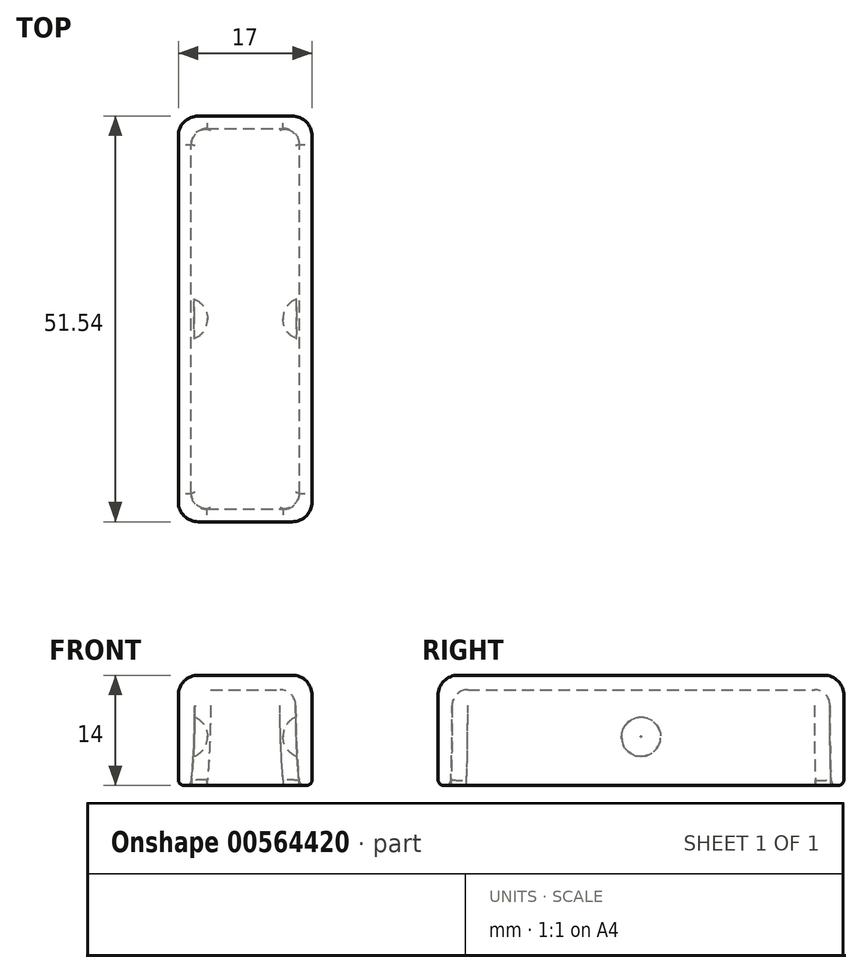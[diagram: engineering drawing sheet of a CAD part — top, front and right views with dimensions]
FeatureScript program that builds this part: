
annotation { "Feature Type Name" : "Feature", "Feature Type Description" : "" }
export const myFeature = defineFeature(function(context is Context, id is Id, definition is map)
    precondition{}
    {
        {
            var Q0;
            Q0=qCreatedBy(makeId("Top.planeOp"),FACE);
            var sketch = newSketch(context, id + "F0", { "sketchPlane" : qUnion([Q0])});
            skLineSegment(sketch, "E0.bottom", {"start": v(39.5, 39.5) * mm, "end": v(-39.5, 39.5) * mm});
            skLineSegment(sketch, "E0.top", {"start": v(39.5, -39.5) * mm, "end": v(-39.5, -39.5) * mm});
            skLineSegment(sketch, "E0.left", {"start": v(39.5, 39.5) * mm, "end": v(39.5, -39.5) * mm});
            skLineSegment(sketch, "E0.right", {"start": v(-39.5, 39.5) * mm, "end": v(-39.5, -39.5) * mm});
            skPoint(sketch, "E0.middle", {"position": v(0, 0) * mm});
            skSolve(sketch);
        }
        {
            var Q0;
            Q0=qSketchRegion(id+"F0",true);
            extrude(context, id + "F1", {"entities" : qUnion([Q0]), "depth" : 50.8 * mm, "offsetDistance" : 25.4 * mm});
        }
        {
            var Q0;
            Q0=makeQuery(id+"F1.opExtrude","SWEPT_FACE",FACE,{"disambiguationData":[OSD([sQuery(id+"F0.wireOp",EDGE,"E0.bottom")])]});
            var sketch = newSketch(context, id + "F2", { "sketchPlane" : qUnion([Q0])});
            skFitSpline(sketch, "E1", {"points": [v(-6.4, 50.8) * mm, v(-11.41, 24.4) * mm, v(-39.5, 10) * mm], "startDerivative": vector(0.05, -69.07) * mm, "endDerivative": vector(-77.08, -18.22) * mm});
            skLineSegment(sketch, "E2", {"start": v(-6.4, 50.8) * mm, "end": v(-39.5, 50.8) * mm});
            skLineSegment(sketch, "E3", {"start": v(-39.5, 50.8) * mm, "end": v(-39.5, 10) * mm});
            skFitSpline(sketch, "E4.MirrorCS", {"points": [v(6.4, 50.8) * mm, v(11.41, 24.4) * mm, v(39.5, 10) * mm], "startDerivative": vector(-0.05, -69.07) * mm, "endDerivative": vector(77.08, -18.22) * mm});
            skLineSegment(sketch, "E5.MirrorCS", {"start": v(6.4, 50.8) * mm, "end": v(39.5, 50.8) * mm});
            skLineSegment(sketch, "E6.MirrorCS", {"start": v(39.5, 50.8) * mm, "end": v(39.5, 10) * mm});
            skSolve(sketch);
        }
        {
            var Q0;
            Q0=qSketchRegion(id+"F2",true);
            extrude(context, id + "F3", {"entities" : qUnion([Q0]), "operationType" : NewBodyOperationType.REMOVE, "endBound" : BoundingType.THROUGH_ALL, "oppositeDirection" : true, "depth" : 25.4 * mm, "offsetDistance" : 25.4 * mm});
        }
        {
            var Q0;
            Q0=makeQuery(id+"F1.opExtrude","CAP_FACE",FACE,{"disambiguationData":[OSD([sQuery(id+"F0.wireOp",EDGE,"E0.bottom"),sQuery(id+"F0.wireOp",EDGE,"E0.top"),sQuery(id+"F0.wireOp",EDGE,"E0.left"),sQuery(id+"F0.wireOp",EDGE,"E0.right")])],"isStart":true});
            var sketch = newSketch(context, id + "F4", { "sketchPlane" : qUnion([Q0])});
            skCircle(sketch, "E7", {"center": v(0, 0) * mm, "radius": 39.5 * mm});
            skSolve(sketch);
        }
        {
            var Q0;
            {var subQ0=sQuery(id+"F4.wireOp",EDGE,"E7");var subQ1=makeQuery(id+"F1.opExtrude","CAP_EDGE",EDGE,{"disambiguationData":[OSD([sQuery(id+"F0.wireOp",EDGE,"E0.left")])],"isStart":true});var subQ2=makeQuery(id+"F4.imprint","INTERSECT",VERTEX,{"derivedFrom":[subQ1,subQ0]});Q0=makeQuery(id+"F4.imprint","IMPRINT",FACE,{"disambiguationData":[TD([[makeQuery(id+"F4.imprint","IMPRINT",EDGE,{"disambiguationData":[TD([[subQ2,1.0]])],"derivedFrom":subQ0}),-1.0]])]});}
            var Q1;
            {var subQ0=sQuery(id+"F4.wireOp",EDGE,"E7");var subQ1=makeQuery(id+"F1.opExtrude","CAP_EDGE",EDGE,{"disambiguationData":[OSD([sQuery(id+"F0.wireOp",EDGE,"E0.right")])],"isStart":true});var subQ2=makeQuery(id+"F4.imprint","INTERSECT",VERTEX,{"derivedFrom":[subQ1,subQ0]});Q1=makeQuery(id+"F4.imprint","IMPRINT",FACE,{"disambiguationData":[TD([[makeQuery(id+"F4.imprint","IMPRINT",EDGE,{"disambiguationData":[TD([[subQ2,-1.0]])],"derivedFrom":subQ0}),-1.0]])]});}
            var Q2;
            {var subQ0=sQuery(id+"F4.wireOp",EDGE,"E7");var subQ1=makeQuery(id+"F1.opExtrude","CAP_EDGE",EDGE,{"disambiguationData":[OSD([sQuery(id+"F0.wireOp",EDGE,"E0.top")])],"isStart":true});var subQ2=makeQuery(id+"F4.imprint","INTERSECT",VERTEX,{"derivedFrom":[subQ1,subQ0]});Q2=makeQuery(id+"F4.imprint","IMPRINT",FACE,{"disambiguationData":[TD([[makeQuery(id+"F4.imprint","IMPRINT",EDGE,{"disambiguationData":[TD([[subQ2,1.0]])],"derivedFrom":subQ0}),-1.0]])]});}
            var Q3;
            {var subQ0=sQuery(id+"F4.wireOp",EDGE,"E7");var subQ1=makeQuery(id+"F1.opExtrude","CAP_EDGE",EDGE,{"disambiguationData":[OSD([sQuery(id+"F0.wireOp",EDGE,"E0.top")])],"isStart":true});var subQ2=makeQuery(id+"F4.imprint","INTERSECT",VERTEX,{"derivedFrom":[subQ1,subQ0]});Q3=makeQuery(id+"F4.imprint","IMPRINT",FACE,{"disambiguationData":[TD([[makeQuery(id+"F4.imprint","IMPRINT",EDGE,{"disambiguationData":[TD([[subQ2,-1.0]])],"derivedFrom":subQ0}),-1.0]])]});}
            extrude(context, id + "F5", {"entities" : qUnion([Q0, Q1, Q2, Q3]), "operationType" : NewBodyOperationType.REMOVE, "endBound" : BoundingType.THROUGH_ALL, "oppositeDirection" : true, "depth" : 25.4 * mm, "offsetDistance" : 25.4 * mm});
        }
        {
            var Q0;
            Q0=qCreatedBy(makeId("Right.planeOp"),FACE);
            var sketch = newSketch(context, id + "F6", { "sketchPlane" : qUnion([Q0])});
            skLineSegment(sketch, "E8.top", {"start": v(24, 50.26) * mm, "end": v(-24, 50.26) * mm});
            skPoint(sketch, "E8.middle", {"position": v(0, 47.85) * mm});
            skPoint(sketch, "E8.bottom.end.orphan", {"position": v(-24, 45.43) * mm});
            skPoint(sketch, "E8.left.start.orphan", {"position": v(24, 45.43) * mm});
            skFitSpline(sketch, "E9", {"points": [v(-24, 50.26) * mm, v(-27.02, 23.49) * mm, v(-39.57, 10) * mm], "startDerivative": vector(-0.16, -57.64) * mm, "endDerivative": vector(-33.37, -21.46) * mm});
            skLineSegment(sketch, "E10", {"start": v(-40.45, 52.33) * mm, "end": v(-43.17, 14.06) * mm});
            skLineSegment(sketch, "E11", {"start": v(-43.17, 14.06) * mm, "end": v(-39.57, 10) * mm});
            skFitSpline(sketch, "E12.MirrorCS", {"points": [v(24, 50.26) * mm, v(27.02, 23.49) * mm, v(39.57, 10) * mm], "startDerivative": vector(0.16, -57.64) * mm, "endDerivative": vector(33.37, -21.46) * mm});
            skLineSegment(sketch, "E13.MirrorCS", {"start": v(40.45, 52.33) * mm, "end": v(43.17, 14.06) * mm});
            skLineSegment(sketch, "E14.MirrorCS", {"start": v(43.17, 14.06) * mm, "end": v(39.57, 10) * mm});
            skLineSegment(sketch, "E15", {"start": v(40.45, 52.33) * mm, "end": v(24, 52.33) * mm});
            skLineSegment(sketch, "E16", {"start": v(24, 52.33) * mm, "end": v(24, 50.26) * mm});
            skLineSegment(sketch, "E17", {"start": v(-24, 52.33) * mm, "end": v(-40.45, 52.33) * mm});
            skLineSegment(sketch, "E18", {"start": v(-24, 52.33) * mm, "end": v(-24, 50.26) * mm});
            skLineSegment(sketch, "E19", {"start": v(-24, 52.33) * mm, "end": v(24, 52.33) * mm});
            skSolve(sketch);
        }
        {
            var Q0;
            Q0=qSketchRegion(id+"F6",true);
            extrude(context, id + "F7", {"entities" : qUnion([Q0]), "operationType" : NewBodyOperationType.REMOVE, "endBound" : BoundingType.THROUGH_ALL, "oppositeDirection" : true, "depth" : 25.4 * mm, "offsetDistance" : 25.4 * mm, "hasSecondDirection" : true, "secondDirectionBound" : SecondDirectionBoundingType.THROUGH_ALL, "secondDirectionOppositeDirection" : false, "secondDirectionDepth" : 25.4 * mm});
        }
        {
            var Q0;
            Q0=makeQuery(id+"F3.boolean.opBoolean","COPY",FACE,{"derivedFrom":makeQuery(id+"F3.opExtrude","SWEPT_FACE",FACE,{"disambiguationData":[OSD([sQuery(id+"F2.wireOp",EDGE,"E4.MirrorCS")])]})});
            var Q1;
            Q1=makeQuery(id+"F7.boolean.opBoolean","COPY",FACE,{"derivedFrom":makeQuery(id+"F7.opExtrude","SWEPT_FACE",FACE,{"disambiguationData":[OSD([sQuery(id+"F6.wireOp",EDGE,"E9")])]})});
            var Q2;
            Q2=makeQuery(id+"F3.boolean.opBoolean","COPY",FACE,{"derivedFrom":makeQuery(id+"F3.opExtrude","SWEPT_FACE",FACE,{"disambiguationData":[OSD([sQuery(id+"F2.wireOp",EDGE,"E1")])]})});
            var Q3;
            Q3=makeQuery(id+"F7.boolean.opBoolean","COPY",FACE,{"derivedFrom":makeQuery(id+"F7.opExtrude","SWEPT_FACE",FACE,{"disambiguationData":[OSD([sQuery(id+"F6.wireOp",EDGE,"E12.MirrorCS")])]})});
            fillet(context, id + "F8", {"entities" : qUnion([Q0, Q1, Q2, Q3]), "radius" : 2 * mm, "tangentPropagation" : true, "allowEdgeOverflow" : false});
        }
        {
            var Q0;
            Q0=qCreatedBy(makeId("Right.planeOp"),FACE);
            cPlane(context, id + "F9", {"entities" : qUnion([Q0]), "cplaneType" : CPlaneType.OFFSET, "offset" : 6.4 * mm, "width" : 152.4 * mm, "height" : 152.4 * mm});
        }
        {
            var Q0;
            Q0=qCreatedBy(id+"F9.planeOp",FACE);
            var sketch = newSketch(context, id + "F10", { "sketchPlane" : qUnion([Q0])});
            skCircle(sketch, "E20", {"center": v(0, 44.28) * mm, "radius": 2.5 * mm});
            skSolve(sketch);
        }
        {
            var Q0;
            Q0=qSketchRegion(id+"F10",true);
            extrude(context, id + "F11", {"entities" : qUnion([Q0]), "operationType" : NewBodyOperationType.REMOVE, "oppositeDirection" : true, "depth" : 1.6 * mm, "offsetDistance" : 25.4 * mm, "hasSecondDirection" : true, "secondDirectionBound" : SecondDirectionBoundingType.THROUGH_ALL, "secondDirectionOppositeDirection" : false, "secondDirectionDepth" : 25.4 * mm});
        }
        {
            var Q0;
            Q0=qCreatedBy(makeId("Right.planeOp"),FACE);
            cPlane(context, id + "F12", {"entities" : qUnion([Q0]), "cplaneType" : CPlaneType.OFFSET, "offset" : 6.4 * mm, "oppositeDirection" : true, "width" : 152.4 * mm, "height" : 152.4 * mm});
        }
        {
            var Q0;
            Q0=qCreatedBy(id+"F12.planeOp",FACE);
            var sketch = newSketch(context, id + "F13", { "sketchPlane" : qUnion([Q0])});
            skCircle(sketch, "E21", {"center": v(0, 44.28) * mm, "radius": 2.5 * mm});
            skSolve(sketch);
        }
        {
            var Q0;
            Q0=qSketchRegion(id+"F13",true);
            extrude(context, id + "F14", {"entities" : qUnion([Q0]), "operationType" : NewBodyOperationType.REMOVE, "depth" : 1.6 * mm, "offsetDistance" : 25.4 * mm, "hasSecondDirection" : true, "secondDirectionBound" : SecondDirectionBoundingType.THROUGH_ALL, "secondDirectionOppositeDirection" : true, "secondDirectionDepth" : 25.4 * mm});
        }
        {
            var Q0;
            Q0=makeQuery(id+"F11.boolean.opBoolean","COPY",EDGE,{"derivedFrom":makeQuery(id+"F11.opExtrude","CAP_EDGE",EDGE,{"disambiguationData":[OSD([sQuery(id+"F10.wireOp",EDGE,"E20")])],"isStart":false})});
            var Q1;
            Q1=makeQuery(id+"F14.boolean.opBoolean","COPY",FACE,{"derivedFrom":makeQuery(id+"F14.opExtrude","CAP_FACE",FACE,{"disambiguationData":[OSD([sQuery(id+"F13.wireOp",EDGE,"E21")])],"isStart":false})});
            fillet(context, id + "F15", {"entities" : qUnion([Q0, Q1]), "radius" : 2.6 * mm, "tangentPropagation" : true, "allowEdgeOverflow" : false});
        }
        {
            var Q0;
            Q0=qCreatedBy(makeId("Right.planeOp"),FACE);
            var sketch = newSketch(context, id + "F16", { "sketchPlane" : qUnion([Q0])});
            skLineSegment(sketch, "E22.bottom", {"start": v(-49.5, 0) * mm, "end": v(46.69, 0) * mm});
            skLineSegment(sketch, "E22.top", {"start": v(-49.5, 38.1) * mm, "end": v(46.69, 38.1) * mm});
            skLineSegment(sketch, "E22.left", {"start": v(-49.5, 0) * mm, "end": v(-49.5, 38.1) * mm});
            skLineSegment(sketch, "E22.right", {"start": v(46.69, 0) * mm, "end": v(46.69, 38.1) * mm});
            skSolve(sketch);
        }
        {
            var Q0;
            Q0 = qSketchRegion(id + "F16", true);
            extrude(context, id + "F17", {"entities" : qUnion([Q0]), "operationType" : NewBodyOperationType.REMOVE, "endBound" : BoundingType.THROUGH_ALL, "oppositeDirection" : true, "depth" : 25.4 * mm, "offsetDistance" : 25.4 * mm, "hasSecondDirection" : true, "secondDirectionBound" : SecondDirectionBoundingType.THROUGH_ALL, "secondDirectionOppositeDirection" : false, "secondDirectionDepth" : 25.4 * mm});
        }
        {
            var Q0;
            Q0=makeQuery(id+"F1.opExtrude","SWEPT_BODY",BODY,{"disambiguationData":[OSD([sQuery(id+"F0.wireOp",EDGE,"E0.bottom"),sQuery(id+"F0.wireOp",EDGE,"E0.top"),sQuery(id+"F0.wireOp",EDGE,"E0.left"),sQuery(id+"F0.wireOp",EDGE,"E0.right")])]});
            transform(context, id + "F18", {"entities" : qUnion([Q0]), "transformType" : TransformType.TRANSLATION_3D, "dx" : 0 * mm, "dy" : 0 * mm, "dz" : 0 * mm, "makeCopy" : true});
        }
        {
            var Q0;
            Q0=makeQuery(id+"F18.opPattern","COPY",FACE,{"derivedFrom":makeQuery(id+"F17.boolean.opBoolean","COPY",FACE,{"derivedFrom":makeQuery(id+"F17.opExtrude","SWEPT_FACE",FACE,{"disambiguationData":[OSD([sQuery(id+"F16.wireOp",EDGE,"E22.top")])]})}),"instanceName":"1"});
            cPlane(context, id + "F19", {"entities" : qUnion([Q0]), "cplaneType" : CPlaneType.OFFSET, "offset" : 0 * mm, "width" : 152.4 * mm, "height" : 152.4 * mm});
        }
        {
            var Q0;
            Q0=qCreatedBy(id+"F19.planeOp",FACE);
            var sketch = newSketch(context, id + "F20", { "sketchPlane" : qUnion([Q0])});
            skLineSegment(sketch, "E23.bottom", {"start": v(8.5, -25.77) * mm, "end": v(-8.5, -25.77) * mm});
            skLineSegment(sketch, "E23.top", {"start": v(8.5, 25.77) * mm, "end": v(-8.5, 25.77) * mm});
            skLineSegment(sketch, "E23.left", {"start": v(8.5, -25.77) * mm, "end": v(8.5, 25.77) * mm});
            skLineSegment(sketch, "E23.right", {"start": v(-8.5, -25.77) * mm, "end": v(-8.5, 25.77) * mm});
            skPoint(sketch, "E23.middle", {"position": v(0, 0) * mm});
            skSolve(sketch);
        }
        {
            var Q0;
            Q0 = qSketchRegion(id + "F20", true);
            extrude(context, id + "F21", {"entities" : qUnion([Q0]), "oppositeDirection" : true, "depth" : 14 * mm, "offsetDistance" : 25.4 * mm});
        }
        {
            var Q0;
            Q0=makeQuery(id+"F21.opExtrude","SWEPT_EDGE",EDGE,{"disambiguationData":[OSD([sQuery(id+"F20.wireOp",EDGE,"E23.top"),sQuery(id+"F20.wireOp",EDGE,"E23.left")])]});
            var Q1;
            Q1=makeQuery(id+"F21.opExtrude","CAP_EDGE",EDGE,{"disambiguationData":[OSD([sQuery(id+"F20.wireOp",EDGE,"E23.left")])],"isStart":false});
            var Q2;
            Q2=makeQuery(id+"F21.opExtrude","CAP_EDGE",EDGE,{"disambiguationData":[OSD([sQuery(id+"F20.wireOp",EDGE,"E23.top")])],"isStart":false});
            var Q3;
            Q3=makeQuery(id+"F21.opExtrude","SWEPT_EDGE",EDGE,{"disambiguationData":[OSD([sQuery(id+"F20.wireOp",EDGE,"E23.top"),sQuery(id+"F20.wireOp",EDGE,"E23.right")])]});
            var Q4;
            Q4=makeQuery(id+"F21.opExtrude","CAP_EDGE",EDGE,{"disambiguationData":[OSD([sQuery(id+"F20.wireOp",EDGE,"E23.right")])],"isStart":false});
            var Q5;
            Q5=makeQuery(id+"F21.opExtrude","SWEPT_EDGE",EDGE,{"disambiguationData":[OSD([sQuery(id+"F20.wireOp",EDGE,"E23.bottom"),sQuery(id+"F20.wireOp",EDGE,"E23.left")])]});
            var Q6;
            Q6=makeQuery(id+"F21.opExtrude","CAP_EDGE",EDGE,{"disambiguationData":[OSD([sQuery(id+"F20.wireOp",EDGE,"E23.bottom")])],"isStart":false});
            var Q7;
            Q7=makeQuery(id+"F21.opExtrude","SWEPT_EDGE",EDGE,{"disambiguationData":[OSD([sQuery(id+"F20.wireOp",EDGE,"E23.bottom"),sQuery(id+"F20.wireOp",EDGE,"E23.right")])]});
            fillet(context, id + "F22", {"entities" : qUnion([Q0, Q1, Q2, Q3, Q4, Q5, Q6, Q7]), "radius" : 2.54 * mm, "tangentPropagation" : true, "allowEdgeOverflow" : false});
        }
        {
            var Q0;
            Q0=makeQuery(id+"F18.opPattern","COPY",BODY,{"derivedFrom":makeQuery(id+"F1.opExtrude","SWEPT_BODY",BODY,{"disambiguationData":[OSD([sQuery(id+"F0.wireOp",EDGE,"E0.bottom"),sQuery(id+"F0.wireOp",EDGE,"E0.top"),sQuery(id+"F0.wireOp",EDGE,"E0.left"),sQuery(id+"F0.wireOp",EDGE,"E0.right")])]}),"instanceName":"1"});
            var Q1;
            Q1=makeQuery(id+"F21.opExtrude","SWEPT_BODY",BODY,{"disambiguationData":[OSD([sQuery(id+"F20.wireOp",EDGE,"E23.bottom"),sQuery(id+"F20.wireOp",EDGE,"E23.top"),sQuery(id+"F20.wireOp",EDGE,"E23.left"),sQuery(id+"F20.wireOp",EDGE,"E23.right")])]});
            booleanBodies(context, id + "F23", {"operationType" : BooleanOperationType.SUBTRACTION, "tools" : qUnion([Q0]), "targets" : qUnion([Q1]), "offsetAll" : true});
        }
        {
            var Q0;
            Q0=makeQuery(id+"F21.opExtrude","CAP_FACE",FACE,{"disambiguationData":[OSD([sQuery(id+"F20.wireOp",EDGE,"E23.bottom"),sQuery(id+"F20.wireOp",EDGE,"E23.top"),sQuery(id+"F20.wireOp",EDGE,"E23.left"),sQuery(id+"F20.wireOp",EDGE,"E23.right")])],"isStart":true});
            fillet(context, id + "F24", {"entities" : qUnion([Q0]), "radius" : .75 * mm, "tangentPropagation" : true, "allowEdgeOverflow" : false});
        }
    });
